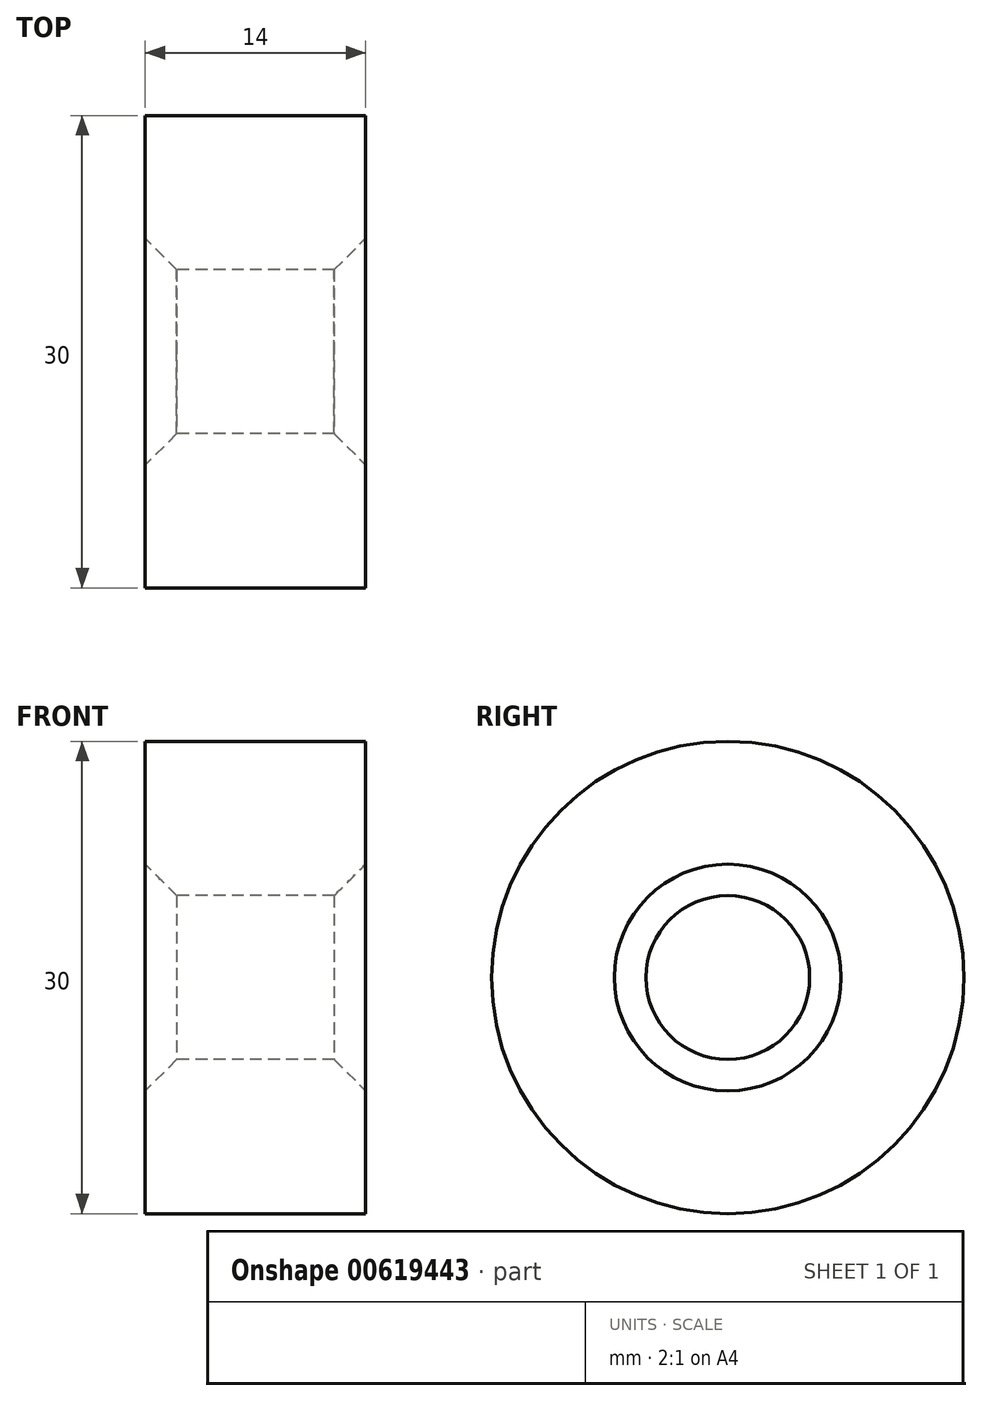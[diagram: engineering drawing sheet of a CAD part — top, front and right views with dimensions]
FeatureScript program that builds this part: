
annotation { "Feature Type Name" : "Feature", "Feature Type Description" : "" }
export const myFeature = defineFeature(function(context is Context, id is Id, definition is map)
    precondition{}
    {
        {
            var Q0;
            Q0=qCreatedBy(makeId("Front.planeOp"),FACE);
            var sketch = newSketch(context, id + "F0", { "sketchPlane" : qUnion([Q0])});
            skLineSegment(sketch, "E0.bottom", {"start": v(0, 0) * mm, "end": v(14, 0) * mm});
            skLineSegment(sketch, "E0.top", {"start": v(0, 15) * mm, "end": v(14, 15) * mm});
            skLineSegment(sketch, "E0.left", {"start": v(0, 0) * mm, "end": v(0, 15) * mm});
            skLineSegment(sketch, "E0.right", {"start": v(14, 0) * mm, "end": v(14, 15) * mm});
            skLineSegment(sketch, "E1.top", {"start": v(0, 5.2) * mm, "end": v(14, 5.2) * mm});
            skLineSegment(sketch, "E1.left", {"start": v(0, 0) * mm, "end": v(0, 5.2) * mm});
            skLineSegment(sketch, "E1.right", {"start": v(14, 0) * mm, "end": v(14, 5.2) * mm});
            skSolve(sketch);
        }
        {
            var Q0;
            Q0=makeQuery(id+"F0.imprint","IMPRINT",FACE,{"disambiguationData":[TD([[makeQuery(id+"F0.imprint","IMPRINT",EDGE,{"derivedFrom":sQuery(id+"F0.wireOp",EDGE,"E0.top")}),-1.0]])]});
            var Q1;
            Q1=sQuery(id+"F0.wireOp",EDGE,"E0.bottom");
            revolve(context, id + "F1", {"entities" : qUnion([Q0]), "axis" : qUnion([Q1]), "revolveType" : RevolveType.FULL});
        }
        {
            var Q0;
            Q0=makeQuery(id+"F1.opRevolve","SWEPT_EDGE",EDGE,{"disambiguationData":[OSD([sQuery(id+"F0.wireOp",EDGE,"E0.left"),sQuery(id+"F0.wireOp",EDGE,"E1.top"),sQuery(id+"F0.wireOp",EDGE,"E1.left")])]});
            var Q1;
            Q1=makeQuery(id+"F1.opRevolve","SWEPT_EDGE",EDGE,{"disambiguationData":[OSD([sQuery(id+"F0.wireOp",EDGE,"E0.right"),sQuery(id+"F0.wireOp",EDGE,"E1.top"),sQuery(id+"F0.wireOp",EDGE,"E1.right")])]});
            chamfer(context, id + "F2", {"entities" : qUnion([Q0, Q1]), "width" : 2 * mm, "tangentPropagation" : true});
        }
    });
